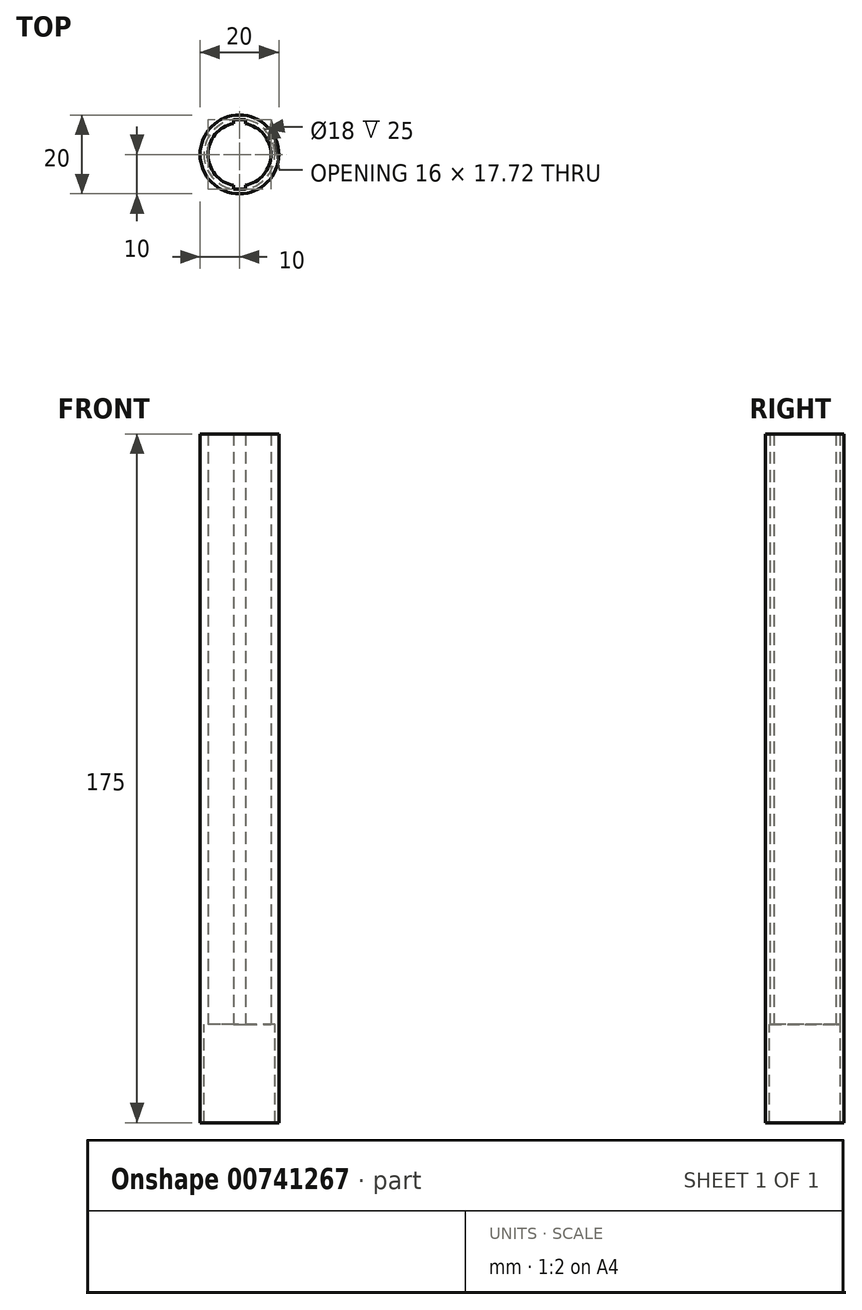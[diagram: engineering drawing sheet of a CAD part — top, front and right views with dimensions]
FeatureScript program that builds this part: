
annotation { "Feature Type Name" : "Feature", "Feature Type Description" : "" }
export const myFeature = defineFeature(function(context is Context, id is Id, definition is map)
    precondition{}
    {
        {
            var Q0;
            Q0=qCreatedBy(makeId("Top.planeOp"),FACE);
            var sketch = newSketch(context, id + "F0", { "sketchPlane" : qUnion([Q0])});
            skCircle(sketch, "E0", {"center": v(0, 0) * mm, "radius": 10 * mm});
            skCircle(sketch, "E1", {"center": v(0, 0) * mm, "radius": 8 * mm});
            skLineSegment(sketch, "E2", {"start": v(-1.5, -7.86) * mm, "end": v(-1.5, -8.86) * mm});
            skLineSegment(sketch, "E3", {"start": v(-1.5, -8.86) * mm, "end": v(1.5, -8.86) * mm});
            skLineSegment(sketch, "E4", {"start": v(1.5, -8.86) * mm, "end": v(1.5, -7.86) * mm});
            skLineSegment(sketch, "E5", {"start": v(-8, 0) * mm, "end": v(8, 0) * mm});
            skLineSegment(sketch, "E6.MirrorCS", {"start": v(1.5, 8.86) * mm, "end": v(1.5, 7.86) * mm});
            skLineSegment(sketch, "E7.MirrorCS", {"start": v(-1.5, 8.86) * mm, "end": v(1.5, 8.86) * mm});
            skLineSegment(sketch, "E8.MirrorCS", {"start": v(-1.5, 7.86) * mm, "end": v(-1.5, 8.86) * mm});
            skCircle(sketch, "E9", {"center": v(0, 0) * mm, "radius": 9 * mm});
            skSolve(sketch);
        }
        {
            var Q0;
            Q0=makeQuery(id+"F0.imprint","IMPRINT",FACE,{"disambiguationData":[TD([[makeQuery(id+"F0.imprint","IMPRINT",EDGE,{"derivedFrom":sQuery(id+"F0.wireOp",EDGE,"E0")}),1.0]])]});
            var Q1;
            {var subQ3=sQuery(id+"F0.wireOp",EDGE,"E2");Q1=makeQuery(id+"F0.imprint","IMPRINT",FACE,{"disambiguationData":[TD([[makeQuery(id+"F0.imprint","IMPRINT",EDGE,{"derivedFrom":subQ3}),-1.0]])]});}
            extrude(context, id + "F1", {"entities" : qUnion([Q0, Q1]), "depth" : 150 * mm, "offsetDistance" : 25 * mm});
        }
        {
            var Q0;
            Q0=makeQuery(id+"F0.imprint","IMPRINT",FACE,{"disambiguationData":[TD([[makeQuery(id+"F0.imprint","IMPRINT",EDGE,{"derivedFrom":sQuery(id+"F0.wireOp",EDGE,"E0")}),1.0]])]});
            extrude(context, id + "F2", {"entities" : qUnion([Q0]), "operationType" : NewBodyOperationType.ADD, "oppositeDirection" : true, "depth" : 25 * mm, "offsetDistance" : 25 * mm});
        }
    });
